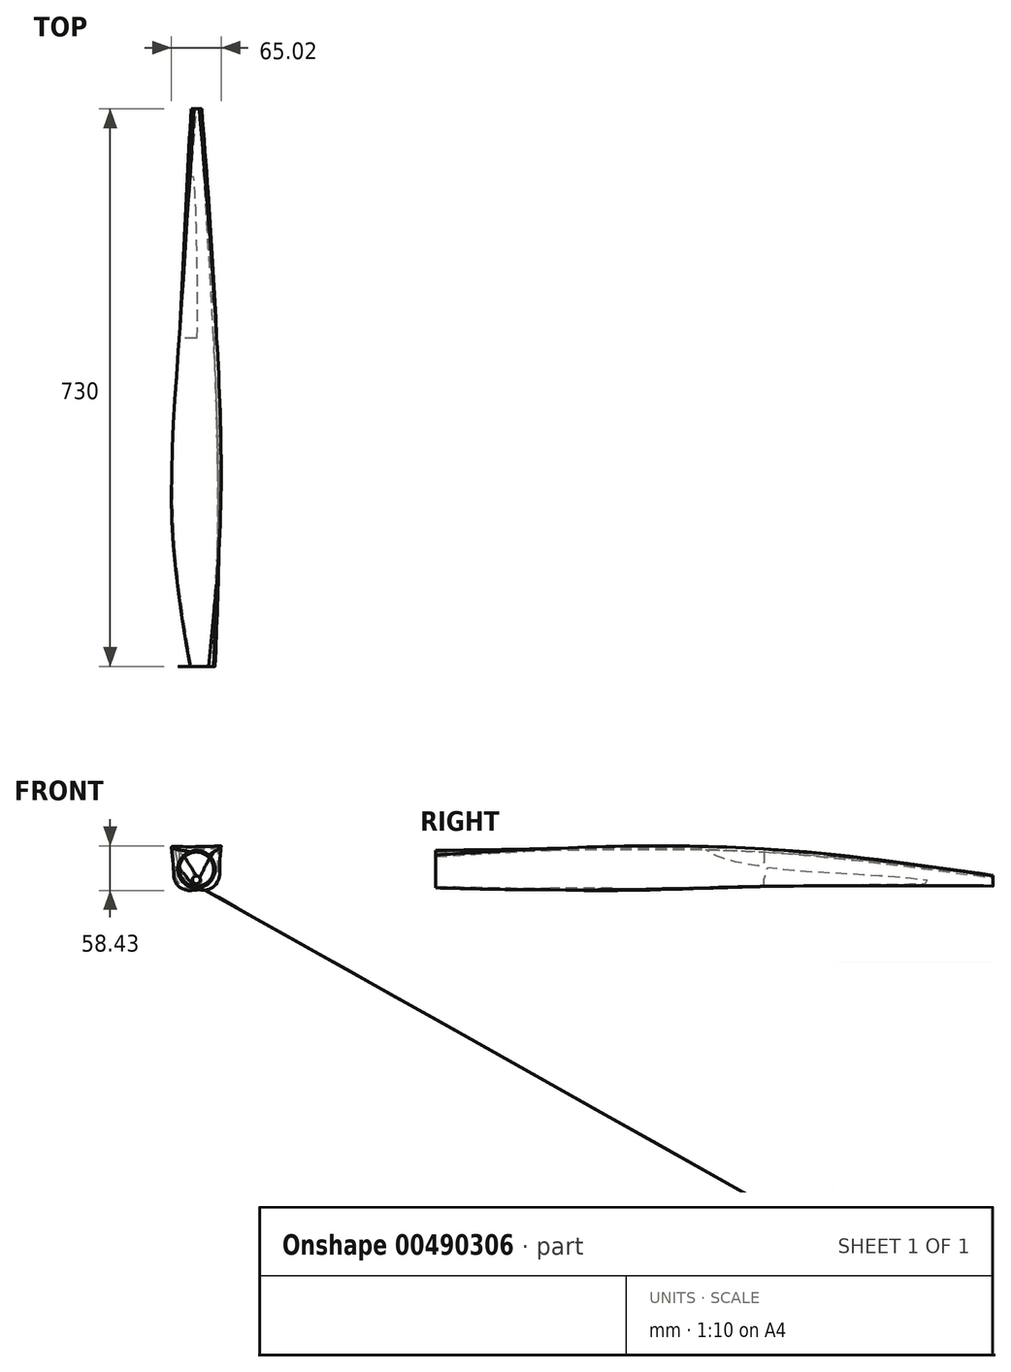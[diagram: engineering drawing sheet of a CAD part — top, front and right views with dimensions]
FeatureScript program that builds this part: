
annotation { "Feature Type Name" : "Feature", "Feature Type Description" : "" }
export const myFeature = defineFeature(function(context is Context, id is Id, definition is map)
    precondition{}
    {
        {
            var Q0;
            Q0=qCreatedBy(makeId("Front.planeOp"),FACE);
            cPlane(context, id + "F0", {"entities" : qUnion([Q0]), "cplaneType" : CPlaneType.OFFSET, "offset" : 150 * mm, "width" : 150 * mm, "height" : 150 * mm});
        }
        {
            var Q0;
            Q0=qCreatedBy(makeId("Front.planeOp"),FACE);
            cPlane(context, id + "F1", {"entities" : qUnion([Q0]), "cplaneType" : CPlaneType.OFFSET, "offset" : 280 * mm, "oppositeDirection" : true, "width" : 150 * mm, "height" : 150 * mm});
        }
        {
            var Q0;
            Q0=qCreatedBy(makeId("Front.planeOp"),FACE);
            cPlane(context, id + "F2", {"entities" : qUnion([Q0]), "cplaneType" : CPlaneType.OFFSET, "offset" : 580 * mm, "oppositeDirection" : true, "width" : 150 * mm, "height" : 150 * mm});
        }
        {
            var Q0;
            Q0=qCreatedBy(id+"F0.planeOp",FACE);
            var sketch = newSketch(context, id + "F3", { "sketchPlane" : qUnion([Q0])});
            skCircle(sketch, "E0", {"center": v(0, 0) * mm, "radius": 22.5 * mm});
            skSolve(sketch);
        }
        {
            var Q0;
            Q0=qCreatedBy(makeId("Front.planeOp"),FACE);
            var sketch = newSketch(context, id + "F4", { "sketchPlane" : qUnion([Q0])});
            skLineSegment(sketch, "E1.bottom", {"start": v(7.5, -25) * mm, "end": v(-7.5, -25) * mm});
            skLineSegment(sketch, "E1.top", {"start": v(27.5, 25) * mm, "end": v(-27.5, 25) * mm});
            skLineSegment(sketch, "E1.left", {"start": v(27.5, -5) * mm, "end": v(27.5, 25) * mm});
            skLineSegment(sketch, "E1.right", {"start": v(-27.5, -5) * mm, "end": v(-27.5, 25) * mm});
            skPoint(sketch, "E1.middle", {"position": v(0, 0) * mm});
            skPoint(sketch, "E2.visualSharp", {"position": v(-27.5, -25) * mm});
            skArc(sketch, "E2.filletArc", {"start": v(-27.5, -5) * mm, "mid": v(-21.64, -19.14) * mm, "end": v(-7.5, -25) * mm});
            skPoint(sketch, "E3.visualSharp", {"position": v(27.5, -25) * mm});
            skArc(sketch, "E3.filletArc", {"start": v(7.5, -25) * mm, "mid": v(21.64, -19.14) * mm, "end": v(27.5, -5) * mm});
            skSolve(sketch);
        }
        {
            var Q0;
            Q0=qCreatedBy(id+"F1.planeOp",FACE);
            var sketch = newSketch(context, id + "F5", { "sketchPlane" : qUnion([Q0])});
            skLineSegment(sketch, "E4.bottom", {"start": v(0, -22.5) * mm, "end": v(0, -22.5) * mm});
            skLineSegment(sketch, "E4.top", {"start": v(22.5, 22.5) * mm, "end": v(-22.5, 22.5) * mm});
            skLineSegment(sketch, "E4.left", {"start": v(22.5, 0) * mm, "end": v(22.5, 22.5) * mm});
            skLineSegment(sketch, "E4.right", {"start": v(-22.5, 0) * mm, "end": v(-22.5, 22.5) * mm});
            skPoint(sketch, "E4.middle", {"position": v(0, 0) * mm});
            skPoint(sketch, "E5.visualSharp", {"position": v(-22.5, -22.5) * mm});
            skArc(sketch, "E5.filletArc", {"start": v(-22.5, 0) * mm, "mid": v(-15.9, -15.9) * mm, "end": v(0, -22.5) * mm});
            skPoint(sketch, "E6.visualSharp", {"position": v(22.5, -22.5) * mm});
            skArc(sketch, "E6.filletArc", {"start": v(0, -22.5) * mm, "mid": v(15.9, -15.9) * mm, "end": v(22.5, 0) * mm});
            skSolve(sketch);
        }
        {
            var Q0;
            Q0=qCreatedBy(id+"F2.planeOp",FACE);
            var sketch = newSketch(context, id + "F6", { "sketchPlane" : qUnion([Q0])});
            skCircle(sketch, "E7", {"center": v(0, -14) * mm, "radius": 5 * mm});
            skSolve(sketch);
        }
        {
            var Q0;
            Q0=makeQuery(id+"F3.imprint","IMPRINT",FACE,{"disambiguationData":[TD([[makeQuery(id+"F3.imprint","IMPRINT",EDGE,{"derivedFrom":sQuery(id+"F3.wireOp",EDGE,"E0")}),1.0]])]});
            var Q1;
            Q1=makeQuery(id+"F4.imprint","IMPRINT",FACE,{"disambiguationData":[TD([[makeQuery(id+"F4.imprint","IMPRINT",EDGE,{"derivedFrom":sQuery(id+"F4.wireOp",EDGE,"E1.bottom")}),-1.0]])]});
            var Q2;
            Q2=makeQuery(id+"F5.imprint","IMPRINT",FACE,{"disambiguationData":[TD([[makeQuery(id+"F5.imprint","IMPRINT",EDGE,{"derivedFrom":sQuery(id+"F5.wireOp",EDGE,"E4.top")}),1.0]])]});
            var Q3;
            Q3=makeQuery(id+"F6.imprint","IMPRINT",FACE,{"disambiguationData":[TD([[makeQuery(id+"F6.imprint","IMPRINT",EDGE,{"derivedFrom":sQuery(id+"F6.wireOp",EDGE,"E7")}),1.0]])]});
            loft(context, id + "F7", {"sheetProfilesArray" : [{ "sheetProfileEntities" : qUnion([Q0]) }, { "sheetProfileEntities" : qUnion([Q1]) }, { "sheetProfileEntities" : qUnion([Q2]) }, { "sheetProfileEntities" : qUnion([Q3]) }]});
        }
        {
            var Q0;
            Q0=qCreatedBy(id+"F0.planeOp",FACE);
            var sketch = newSketch(context, id + "F8", { "sketchPlane" : qUnion([Q0])});
            skCircle(sketch, "E8", {"center": v(0, 0) * mm, "radius": 24.5 * mm});
            skSolve(sketch);
        }
        {
            var Q0;
            Q0=qCreatedBy(makeId("Front.planeOp"),FACE);
            var sketch = newSketch(context, id + "F9", { "sketchPlane" : qUnion([Q0])});
            skLineSegment(sketch, "E9.bottom", {"start": v(9.5, -27) * mm, "end": v(-9.5, -27) * mm});
            skLineSegment(sketch, "E9.top", {"start": v(29.5, 27) * mm, "end": v(-29.5, 27) * mm});
            skLineSegment(sketch, "E9.left", {"start": v(29.5, -7) * mm, "end": v(29.5, 27) * mm});
            skLineSegment(sketch, "E9.right", {"start": v(-29.5, -7) * mm, "end": v(-29.5, 27) * mm});
            skPoint(sketch, "E9.middle", {"position": v(0, 0) * mm});
            skPoint(sketch, "E10.visualSharp", {"position": v(-29.5, -27) * mm});
            skArc(sketch, "E10.filletArc", {"start": v(-29.5, -7) * mm, "mid": v(-23.64, -21.14) * mm, "end": v(-9.5, -27) * mm});
            skPoint(sketch, "E11.visualSharp", {"position": v(29.5, -27) * mm});
            skArc(sketch, "E11.filletArc", {"start": v(9.5, -27) * mm, "mid": v(23.64, -21.14) * mm, "end": v(29.5, -7) * mm});
            skSolve(sketch);
        }
        {
            var Q0;
            Q0=qCreatedBy(id+"F1.planeOp",FACE);
            var sketch = newSketch(context, id + "F10", { "sketchPlane" : qUnion([Q0])});
            skLineSegment(sketch, "E12.bottom", {"start": v(4, -22.5) * mm, "end": v(0, -22.5) * mm});
            skLineSegment(sketch, "E12.top", {"start": v(26.5, 26.5) * mm, "end": v(-22.5, 26.5) * mm});
            skLineSegment(sketch, "E12.left", {"start": v(26.5, 0) * mm, "end": v(26.5, 26.5) * mm});
            skLineSegment(sketch, "E12.right", {"start": v(-22.5, 0) * mm, "end": v(-22.5, 26.5) * mm});
            skPoint(sketch, "E12.middle", {"position": v(2, 2) * mm});
            skPoint(sketch, "E13.visualSharp", {"position": v(-22.5, -22.5) * mm});
            skArc(sketch, "E13.filletArc", {"start": v(-22.5, 0) * mm, "mid": v(-15.9, -15.9) * mm, "end": v(0, -22.5) * mm});
            skPoint(sketch, "E14.visualSharp", {"position": v(26.5, -22.5) * mm});
            skArc(sketch, "E14.filletArc", {"start": v(4, -22.5) * mm, "mid": v(19.9, -15.9) * mm, "end": v(26.5, 0) * mm});
            skSolve(sketch);
        }
        {
            var Q0;
            Q0=qCreatedBy(id+"F2.planeOp",FACE);
            var sketch = newSketch(context, id + "F11", { "sketchPlane" : qUnion([Q0])});
            skCircle(sketch, "E15", {"center": v(0, -15) * mm, "radius": 7 * mm});
            skSolve(sketch);
        }
        {
            var Q1;
            Q1 = qSketchRegion(id + "F8", true);
            var Q2;
            Q2 = qSketchRegion(id + "F9", true);
            var Q3;
            Q3 = qSketchRegion(id + "F10", true);
            var Q4;
            Q4 = qSketchRegion(id + "F11", true);
            loft(context, id + "F12", {"sheetProfilesArray" : [{ "sheetProfileEntities" : qUnion([Q1]) }, { "sheetProfileEntities" : qUnion([Q2]) }, { "sheetProfileEntities" : qUnion([Q3]) }, { "sheetProfileEntities" : qUnion([Q4]) }]});
        }
        {
            var Q0;
            Q0=makeQuery(id+"F7.opLoft","SWEPT_BODY",BODY,{"disambiguationData":[OSD([makeQuery(id+"F3.imprint","IMPRINT",FACE,{"disambiguationData":[TD([[makeQuery(id+"F3.imprint","IMPRINT",EDGE,{"derivedFrom":sQuery(id+"F3.wireOp",EDGE,"E0")}),1.0]])]}),sQuery(id+"F4.wireOp",EDGE,"E1.bottom"),sQuery(id+"F5.wireOp",EDGE,"E5.filletArc"),makeQuery(id+"F6.imprint","IMPRINT",FACE,{"disambiguationData":[TD([[makeQuery(id+"F6.imprint","IMPRINT",EDGE,{"derivedFrom":sQuery(id+"F6.wireOp",EDGE,"E7")}),1.0]])]})])]});
            var Q1;
            Q1=makeQuery(id+"F12.opLoft","SWEPT_BODY",BODY,{"disambiguationData":[OSD([makeQuery(id+"F8.imprint","IMPRINT",FACE,{"disambiguationData":[TD([[makeQuery(id+"F8.imprint","IMPRINT",EDGE,{"derivedFrom":sQuery(id+"F8.wireOp",EDGE,"E8")}),1.0]])]}),sQuery(id+"F9.wireOp",EDGE,"E9.bottom"),sQuery(id+"F10.wireOp",EDGE,"E12.bottom"),makeQuery(id+"F11.imprint","IMPRINT",FACE,{"disambiguationData":[TD([[makeQuery(id+"F11.imprint","IMPRINT",EDGE,{"derivedFrom":sQuery(id+"F11.wireOp",EDGE,"E15")}),1.0]])]})])]});
            booleanBodies(context, id + "F13", {"operationType" : BooleanOperationType.SUBTRACTION, "tools" : qUnion([Q0]), "targets" : qUnion([Q1])});
        }
    });
